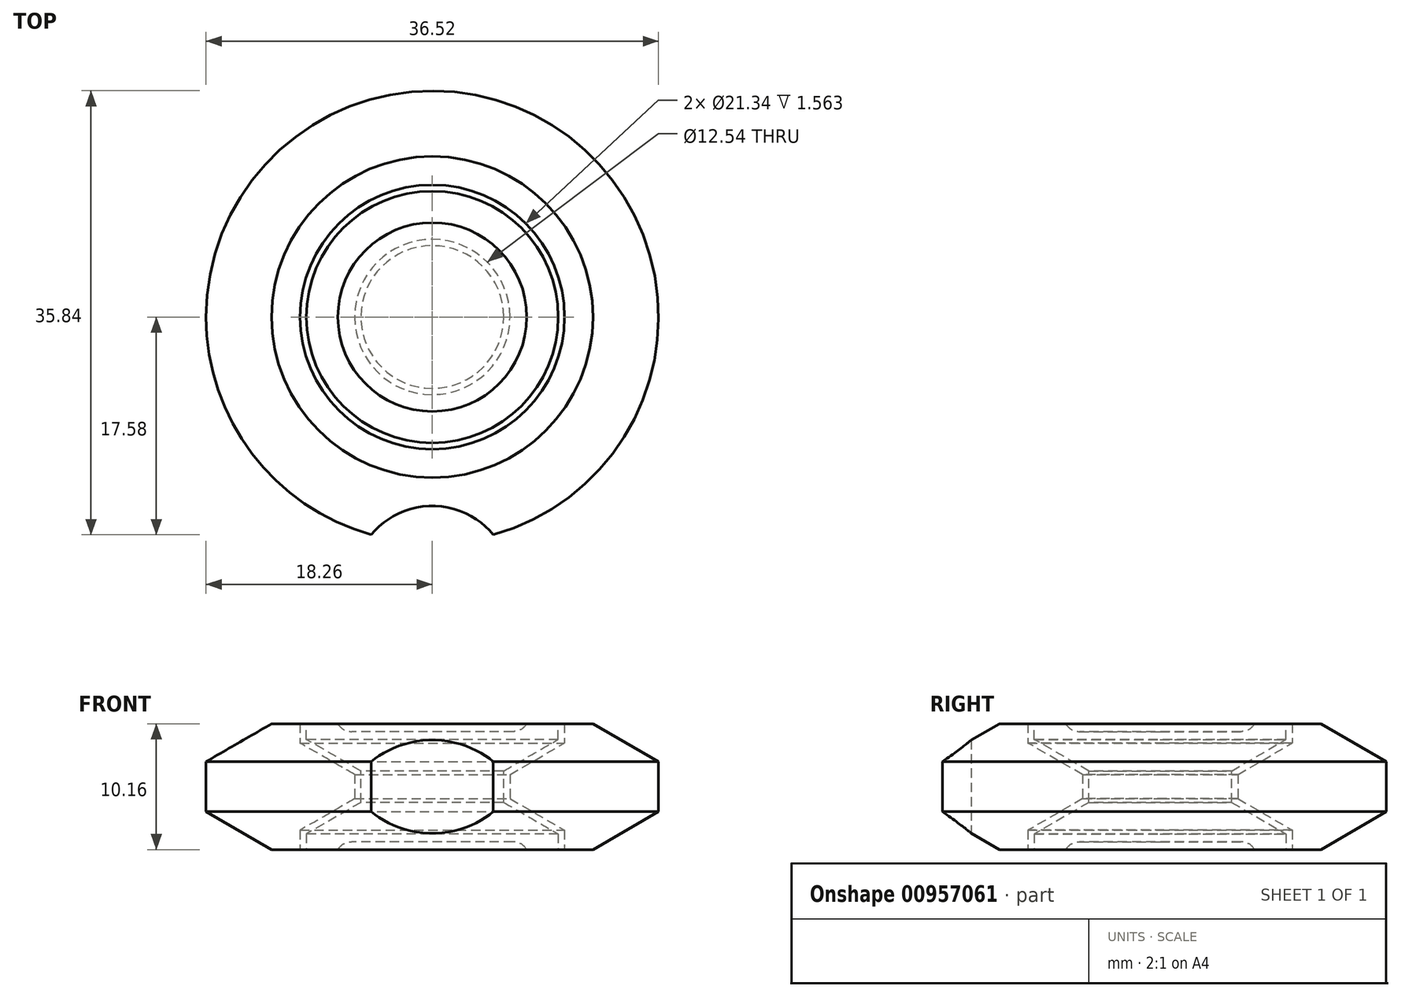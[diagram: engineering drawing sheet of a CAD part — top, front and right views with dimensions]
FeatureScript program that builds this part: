
annotation { "Feature Type Name" : "Feature", "Feature Type Description" : "" }
export const myFeature = defineFeature(function(context is Context, id is Id, definition is map)
    precondition{}
    {
        {
            var Q0;
            Q0=qCreatedBy(makeId("Front.planeOp"),FACE);
            var sketch = newSketch(context, id + "F0", { "sketchPlane" : qUnion([Q0])});
            skLineSegment(sketch, "E0", {"start": v(-5.76, 1.27) * mm, "end": v(-10.16, 3.81) * mm});
            skLineSegment(sketch, "E1", {"start": v(-10.16, 3.81) * mm, "end": v(-10.16, 5.08) * mm});
            skLineSegment(sketch, "E2", {"start": v(-10.16, 5.08) * mm, "end": v(0, 5.08) * mm});
            skLineSegment(sketch, "E3", {"start": v(-5.76, 1.27) * mm, "end": v(-5.76, 0) * mm});
            skLineSegment(sketch, "E4", {"start": v(0, 5.08) * mm, "end": v(0, 0) * mm});
            skLineSegment(sketch, "E5", {"start": v(0, 0) * mm, "end": v(-5.76, 0) * mm});
            skLineSegment(sketch, "E6.MirrorCS", {"start": v(-10.16, -3.81) * mm, "end": v(-10.16, -5.08) * mm});
            skLineSegment(sketch, "E7.MirrorCS", {"start": v(-5.76, -1.27) * mm, "end": v(-5.76, 0) * mm});
            skLineSegment(sketch, "E8.MirrorCS", {"start": v(-5.76, -1.27) * mm, "end": v(-10.16, -3.81) * mm});
            skLineSegment(sketch, "E9.MirrorCS", {"start": v(0, -5.08) * mm, "end": v(0, 0) * mm});
            skLineSegment(sketch, "E10.MirrorCS", {"start": v(-10.16, -5.08) * mm, "end": v(0, -5.08) * mm});
            skSolve(sketch);
        }
        {
            var Q0;
            Q0=makeQuery(id+"F0.imprint","IMPRINT",FACE,{"disambiguationData":[TD([[makeQuery(id+"F0.imprint","IMPRINT",EDGE,{"derivedFrom":sQuery(id+"F0.wireOp",EDGE,"E0")}),-1.0]])]});
            var Q1;
            Q1=sQuery(id+"F0.wireOp",EDGE,"E4");
            revolve(context, id + "F1", {"surfaceOperationType" : NewSurfaceOperationType.NEW, "entities" : qUnion([Q0]), "axis" : qUnion([Q1]), "revolveType" : RevolveType.FULL});
        }
        {
            var Q0;
            Q0=makeQuery(id+"F1.opRevolve","SWEPT_FACE",FACE,{"disambiguationData":[OSD([sQuery(id+"F0.wireOp",EDGE,"E2")])]});
            var sketch = newSketch(context, id + "F2", { "sketchPlane" : qUnion([Q0])});
            skCircle(sketch, "E11", {"center": v(0, 0) * mm, "radius": 7.62 * mm});
            skSolve(sketch);
        }
        {
            var Q0;
            Q0=makeQuery(id+"F2.imprint","IMPRINT",FACE,{"disambiguationData":[TD([[makeQuery(id+"F2.imprint","IMPRINT",EDGE,{"derivedFrom":sQuery(id+"F2.wireOp",EDGE,"E11")}),1.0]])]});
            extrude(context, id + "F3", {"entities" : qUnion([Q0]), "operationType" : NewBodyOperationType.REMOVE, "oppositeDirection" : true, "depth" : 0.64 * mm, "offsetDistance" : 25.4 * mm});
        }
        {
            var Q0;
            Q0=makeQuery(id+"F3.boolean.opBoolean","COPY",EDGE,{"derivedFrom":makeQuery(id+"F3.opExtrude","CAP_EDGE",EDGE,{"disambiguationData":[OSD([sQuery(id+"F2.wireOp",EDGE,"E11")])],"isStart":false})});
            fillet(context, id + "F4", {"entities" : qUnion([Q0]), "radius" : 1.27 * mm, "tangentPropagation" : true, "allowEdgeOverflow" : false});
        }
        {
            var Q0;
            Q0=makeQuery(id+"F1.opRevolve","SWEPT_BODY",BODY,{"disambiguationData":[OSD([sQuery(id+"F0.wireOp",EDGE,"E0"),sQuery(id+"F0.wireOp",EDGE,"E1"),sQuery(id+"F0.wireOp",EDGE,"E2"),sQuery(id+"F0.wireOp",EDGE,"E3"),sQuery(id+"F0.wireOp",EDGE,"E4"),sQuery(id+"F0.wireOp",EDGE,"E5")])]});
            var Q1;
            Q1=makeQuery(id+"F1.opRevolve","SWEPT_FACE",FACE,{"disambiguationData":[OSD([sQuery(id+"F0.wireOp",EDGE,"E5")])]});
            mirror(context, id + "F5", {"operationType" : NewBodyOperationType.ADD, "entities" : qUnion([Q0]), "mirrorPlane" : qUnion([Q1])});
        }
        {
            var Q0;
            Q0=qCreatedBy(makeId("Front.planeOp"),FACE);
            var sketch = newSketch(context, id + "F6", { "sketchPlane" : qUnion([Q0])});
            skLineSegment(sketch, "E12", {"start": v(0, -14.75) * mm, "end": v(0, 13.72) * mm, "construction": true});
            skLineSegment(sketch, "E13", {"start": v(-5.76, -1.27) * mm, "end": v(-5.76, 1.27) * mm, "construction": true});
            skLineSegment(sketch, "E14", {"start": v(-5.76, 1.27) * mm, "end": v(-10.16, 3.81) * mm, "construction": true});
            skLineSegment(sketch, "E15", {"start": v(-10.16, -3.81) * mm, "end": v(-5.76, -1.27) * mm, "construction": true});
            skLineSegment(sketch, "E16", {"start": v(-10.16, -5.08) * mm, "end": v(-10.16, -3.81) * mm, "construction": true});
            skLineSegment(sketch, "E17", {"start": v(-10.16, 3.81) * mm, "end": v(-10.16, 5.08) * mm, "construction": true});
            skLineSegment(sketch, "E18.0", {"start": v(-10.67, 3.52) * mm, "end": v(-10.67, 5.08) * mm});
            skLineSegment(sketch, "E18.1", {"start": v(-10.67, -5.08) * mm, "end": v(-10.67, -3.52) * mm});
            skLineSegment(sketch, "E18.2", {"start": v(-10.67, -3.52) * mm, "end": v(-6.27, -0.98) * mm});
            skLineSegment(sketch, "E18.3", {"start": v(-6.27, -0.98) * mm, "end": v(-6.27, 0.98) * mm});
            skLineSegment(sketch, "E18.4", {"start": v(-6.27, 0.98) * mm, "end": v(-10.67, 3.52) * mm});
            skLineSegment(sketch, "E19", {"start": v(-18.26, 2.02) * mm, "end": v(-18.26, -2.02) * mm});
            skLineSegment(sketch, "E20", {"start": v(-18.26, 2.02) * mm, "end": v(-12.96, 5.08) * mm});
            skLineSegment(sketch, "E21", {"start": v(-12.96, 5.08) * mm, "end": v(-10.67, 5.08) * mm});
            skLineSegment(sketch, "E22", {"start": v(-10.67, -5.08) * mm, "end": v(-12.96, -5.08) * mm});
            skLineSegment(sketch, "E23", {"start": v(-12.96, -5.08) * mm, "end": v(-18.26, -2.02) * mm});
            skSolve(sketch);
        }
        {
            var Q0;
            Q0 = qSketchRegion(id + "F6", true);
            var Q1;
            Q1=sQuery(id+"F6.wireOp",EDGE,"E12");
            revolve(context, id + "F7", {"surfaceOperationType" : NewSurfaceOperationType.NEW, "entities" : qUnion([Q0]), "axis" : qUnion([Q1]), "revolveType" : RevolveType.FULL});
        }
        {
            var Q0;
            Q0=qCreatedBy(makeId("Top.planeOp"),FACE);
            var sketch = newSketch(context, id + "F8", { "sketchPlane" : qUnion([Q0])});
            skCircle(sketch, "E24", {"center": v(0, -21.59) * mm, "radius": 6.35 * mm});
            skSolve(sketch);
        }
        {
            var Q0;
            Q0 = qSketchRegion(id + "F8", true);
            extrude(context, id + "F9", {"entities" : qUnion([Q0]), "operationType" : NewBodyOperationType.REMOVE, "endBound" : BoundingType.THROUGH_ALL, "depth" : 25.4 * mm, "offsetDistance" : 25.4 * mm, "hasSecondDirection" : true, "secondDirectionBound" : SecondDirectionBoundingType.THROUGH_ALL, "secondDirectionOppositeDirection" : true, "secondDirectionDepth" : 25.4 * mm});
        }
    });
